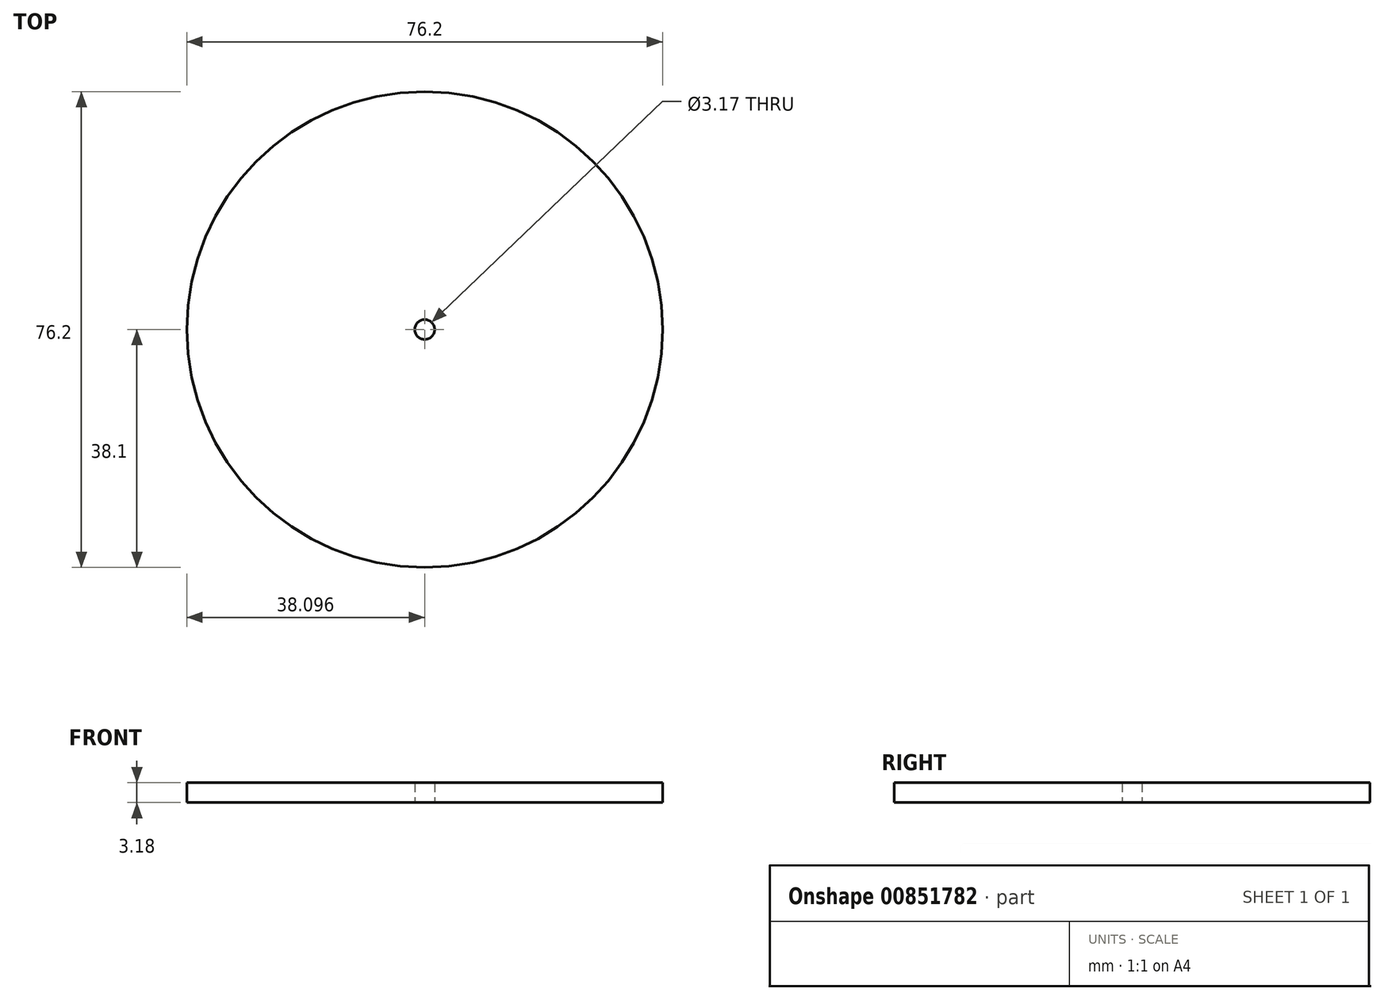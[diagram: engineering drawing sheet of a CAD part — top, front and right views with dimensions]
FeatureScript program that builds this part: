
annotation { "Feature Type Name" : "Feature", "Feature Type Description" : "" }
export const myFeature = defineFeature(function(context is Context, id is Id, definition is map)
    precondition{}
    {
        {
            var Q0;
            Q0=qCreatedBy(makeId("Top.planeOp"),FACE);
            var sketch = newSketch(context, id + "F0", { "sketchPlane" : qUnion([Q0])});
            skCircle(sketch, "E0", {"center": v(1.5, 0) * mm, "radius": 38.1 * mm});
            skCircle(sketch, "E1", {"center": v(1.5, 0) * mm, "radius": 1.59 * mm});
            skSolve(sketch);
        }
        {
            var Q0;
            Q0=makeQuery(id+"F0.imprint","IMPRINT",FACE,{"disambiguationData":[TD([[makeQuery(id+"F0.imprint","IMPRINT",EDGE,{"derivedFrom":sQuery(id+"F0.wireOp",EDGE,"E0")}),1.0]])]});
            extrude(context, id + "F1", {"entities" : qUnion([Q0]), "depth" : 3.17 * mm, "offsetDistance" : 25.4 * mm});
        }
    });
